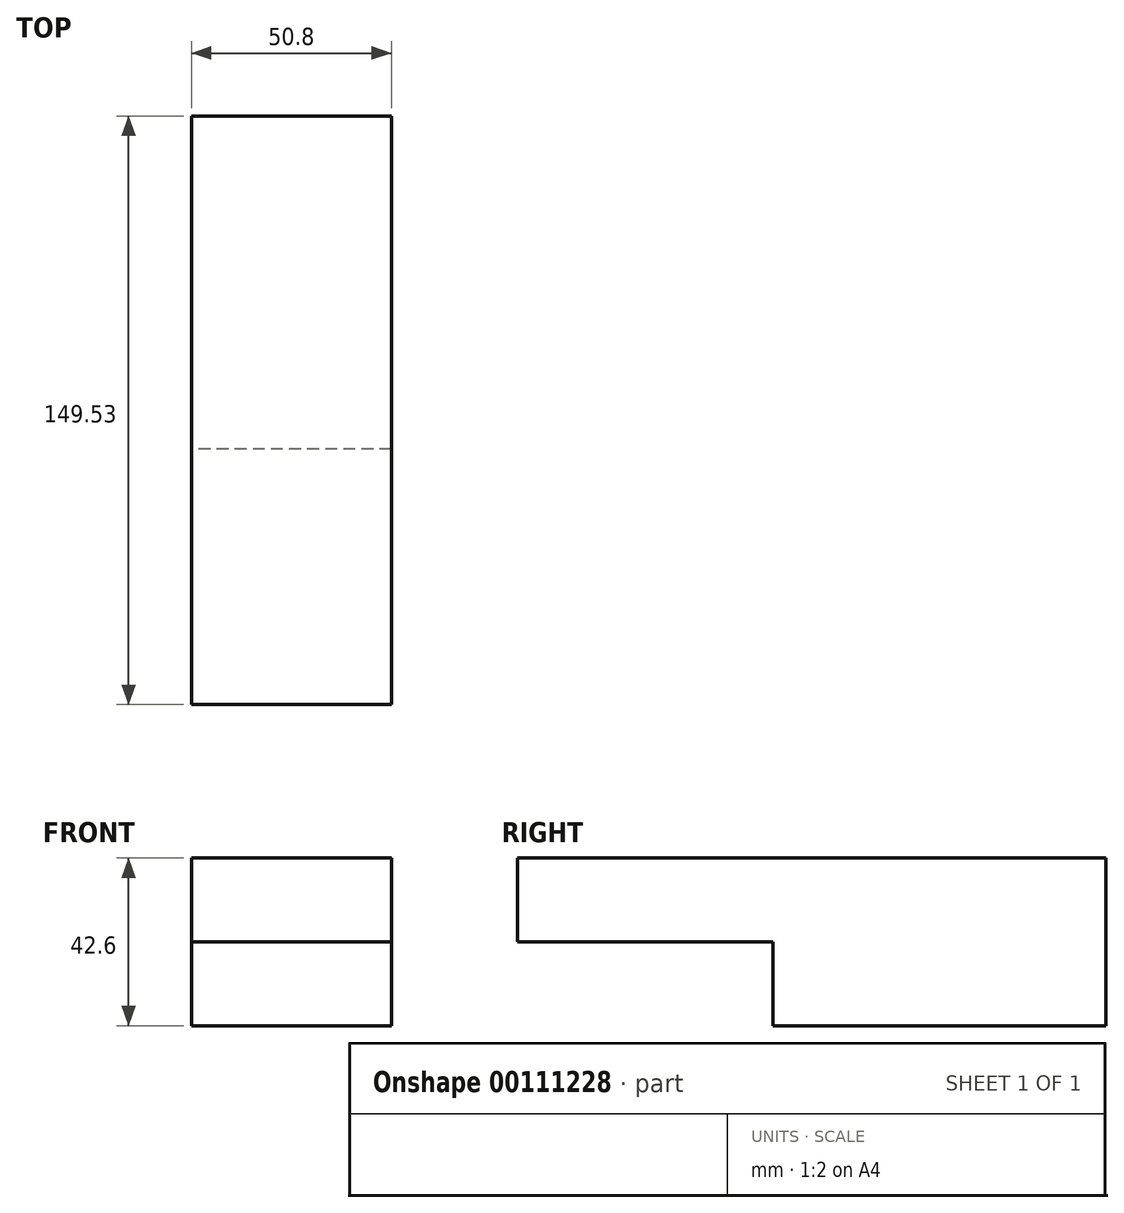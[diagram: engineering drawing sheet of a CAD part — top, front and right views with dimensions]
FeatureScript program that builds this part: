
annotation { "Feature Type Name" : "Feature", "Feature Type Description" : "" }
export const myFeature = defineFeature(function(context is Context, id is Id, definition is map)
    precondition{}
    {
        {
            var Q0;
            Q0=qCreatedBy(makeId("Right.planeOp"),FACE);
            var sketch = newSketch(context, id + "F0", { "sketchPlane" : qUnion([Q0])});
            skLineSegment(sketch, "E0.bottom", {"start": v(42.3, 21.3) * mm, "end": v(-42.3, 21.3) * mm});
            skLineSegment(sketch, "E0.top", {"start": v(42.3, -21.3) * mm, "end": v(-42.3, -21.3) * mm});
            skLineSegment(sketch, "E0.left", {"start": v(42.3, 21.3) * mm, "end": v(42.3, -21.3) * mm});
            skLineSegment(sketch, "E0.right", {"start": v(-42.3, 21.3) * mm, "end": v(-42.3, -21.3) * mm});
            skPoint(sketch, "E0.middle", {"position": v(0, 0) * mm});
            skLineSegment(sketch, "E1.bottom", {"start": v(-42.3, 21.3) * mm, "end": v(-107.23, 21.3) * mm});
            skLineSegment(sketch, "E1.top", {"start": v(-42.3, 0) * mm, "end": v(-107.23, 0) * mm});
            skLineSegment(sketch, "E1.left", {"start": v(-42.3, 21.3) * mm, "end": v(-42.3, 0) * mm});
            skLineSegment(sketch, "E1.right", {"start": v(-107.23, 21.3) * mm, "end": v(-107.23, 0) * mm});
            skPoint(sketch, "E2.oppositeSnap0", {"position": v(0, 21.3) * mm});
            skLineSegment(sketch, "E2.bottom", {"start": v(4.88, 21.3) * mm, "end": v(0, 21.3) * mm});
            skLineSegment(sketch, "E2.top", {"start": v(4.88, 31.35) * mm, "end": v(0, 31.35) * mm});
            skLineSegment(sketch, "E2.left", {"start": v(4.88, 21.3) * mm, "end": v(4.88, 31.35) * mm});
            skLineSegment(sketch, "E2.right", {"start": v(0, 21.3) * mm, "end": v(0, 31.35) * mm});
            skSolve(sketch);
        }
        {
            var Q0;
            Q0=makeQuery(id+"F0.imprint","IMPRINT",FACE,{"disambiguationData":[TD([[makeQuery(id+"F0.imprint","IMPRINT",EDGE,{"derivedFrom":sQuery(id+"F0.wireOp",EDGE,"E0.top")}),-1.0]])]});
            var Q1;
            Q1=makeQuery(id+"F0.imprint","IMPRINT",FACE,{"disambiguationData":[TD([[makeQuery(id+"F0.imprint","IMPRINT",EDGE,{"derivedFrom":sQuery(id+"F0.wireOp",EDGE,"E1.bottom")}),1.0]])]});
            var Q2;
            Q2=makeQuery(id+"F0.imprint","IMPRINT",FACE,{"disambiguationData":[TD([[makeQuery(id+"F0.imprint","IMPRINT",EDGE,{"derivedFrom":sQuery(id+"F0.wireOp",EDGE,"E2.bottom")}),-1.0]])]});
            extrude(context, id + "F1", {"entities" : qUnion([Q0, Q1, Q2]), "depth" : 25.4 * mm});
        }
        {
            var Q0;
            Q0=makeQuery(id+"F1.opExtrude","CAP_FACE",FACE,{"disambiguationData":[OSD([sQuery(id+"F0.wireOp",EDGE,"E0.bottom"),sQuery(id+"F0.wireOp",EDGE,"E0.top"),sQuery(id+"F0.wireOp",EDGE,"E0.left"),sQuery(id+"F0.wireOp",EDGE,"E0.right"),sQuery(id+"F0.wireOp",EDGE,"E1.bottom"),sQuery(id+"F0.wireOp",EDGE,"E1.top"),sQuery(id+"F0.wireOp",EDGE,"E1.right"),sQuery(id+"F0.wireOp",EDGE,"E2.top"),sQuery(id+"F0.wireOp",EDGE,"E2.left"),sQuery(id+"F0.wireOp",EDGE,"E2.right")])],"isStart":true});
            extrude(context, id + "F2", {"entities" : qUnion([Q0]), "operationType" : NewBodyOperationType.ADD, "depth" : 25.4 * mm});
        }
    });
